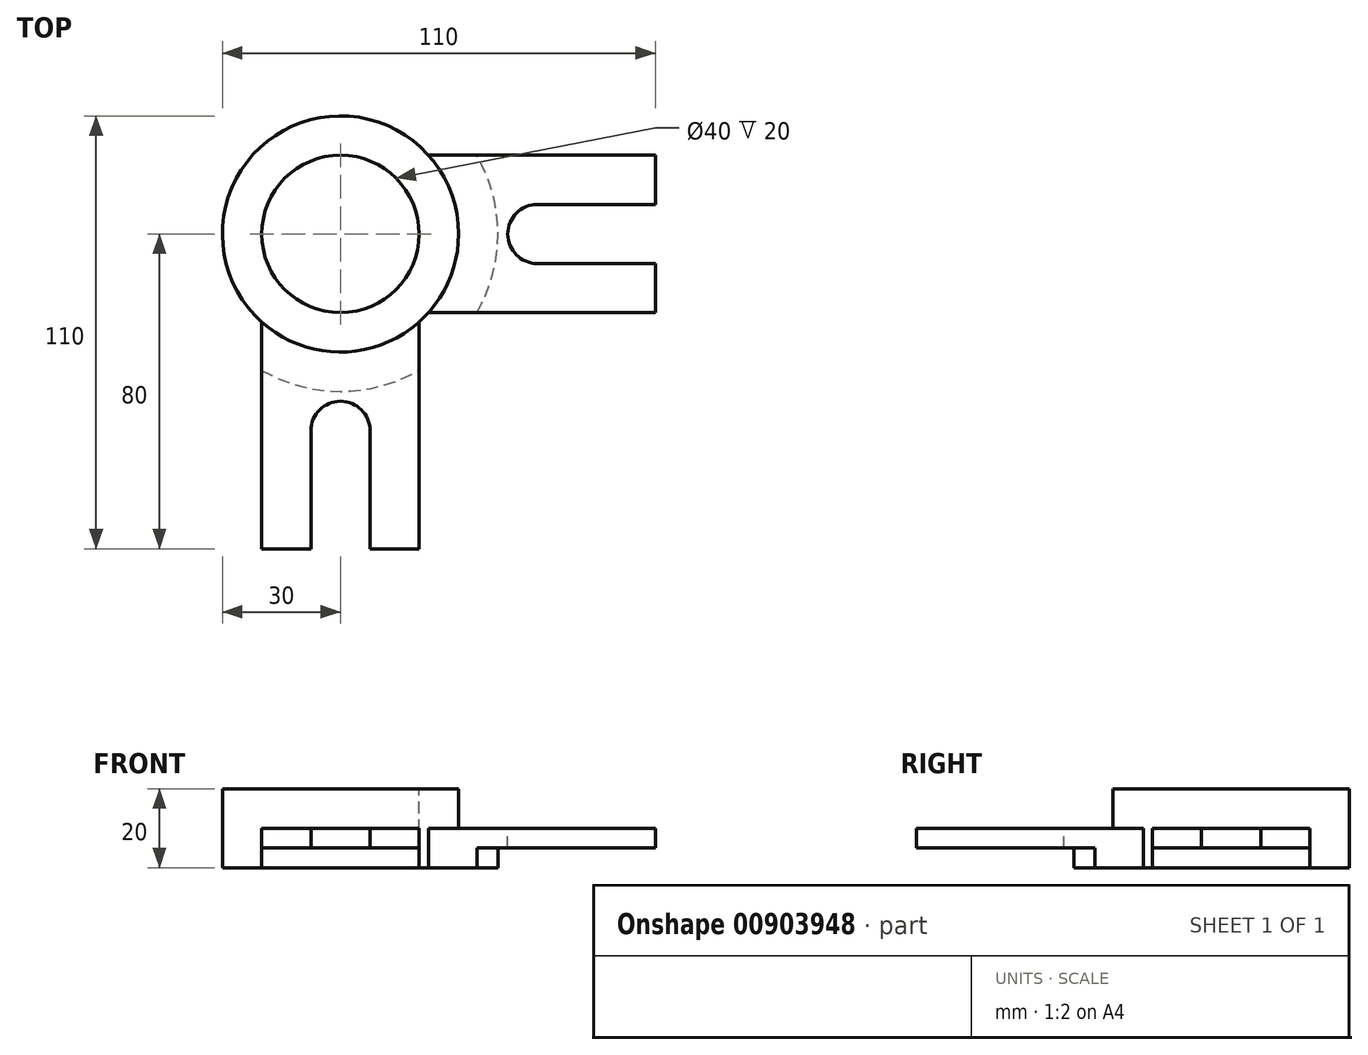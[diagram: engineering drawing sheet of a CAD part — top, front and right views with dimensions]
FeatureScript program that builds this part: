
annotation { "Feature Type Name" : "Feature", "Feature Type Description" : "" }
export const myFeature = defineFeature(function(context is Context, id is Id, definition is map)
    precondition{}
    {
        {
            var Q0;
            Q0=qCreatedBy(makeId("Top.planeOp"),FACE);
            var sketch = newSketch(context, id + "F0", { "sketchPlane" : qUnion([Q0])});
            skCircle(sketch, "E0", {"center": v(0, 0) * mm, "radius": 30 * mm});
            skSolve(sketch);
        }
        {
            var Q0;
            Q0=makeQuery(id+"F0.imprint","IMPRINT",FACE,{"disambiguationData":[TD([[makeQuery(id+"F0.imprint","IMPRINT",EDGE,{"derivedFrom":sQuery(id+"F0.wireOp",EDGE,"E0")}),1.0]])]});
            extrude(context, id + "F1", {"entities" : qUnion([Q0]), "depth" : 20 * mm, "offsetDistance" : 25 * mm});
        }
        {
            var Q0;
            Q0=qCreatedBy(makeId("Top.planeOp"),FACE);
            var sketch = newSketch(context, id + "F2", { "sketchPlane" : qUnion([Q0])});
            skLineSegment(sketch, "E1", {"start": v(0, 0) * mm, "end": v(94.8, 0) * mm, "construction": true});
            skLineSegment(sketch, "E2.bottom", {"start": v(0, 20) * mm, "end": v(80, 20) * mm});
            skLineSegment(sketch, "E2.top", {"start": v(0, -20) * mm, "end": v(80, -20) * mm});
            skLineSegment(sketch, "E2.left", {"start": v(0, 20) * mm, "end": v(0, -20) * mm});
            skLineSegment(sketch, "E2.right", {"start": v(80, 20) * mm, "end": v(80, -20) * mm});
            skSolve(sketch);
        }
        {
            var Q0;
            Q0=makeQuery(id+"F2.imprint","IMPRINT",FACE,{"disambiguationData":[TD([[makeQuery(id+"F2.imprint","IMPRINT",EDGE,{"derivedFrom":sQuery(id+"F2.wireOp",EDGE,"E2.bottom")}),-1.0]])]});
            extrude(context, id + "F3", {"entities" : qUnion([Q0]), "operationType" : NewBodyOperationType.ADD, "depth" : 10 * mm, "offsetDistance" : 25 * mm});
        }
        {
            var Q0;
            Q0=makeQuery(id+"F3.opExtrude","CAP_FACE",FACE,{"disambiguationData":[OSD([sQuery(id+"F2.wireOp",EDGE,"E2.bottom"),sQuery(id+"F2.wireOp",EDGE,"E2.top"),sQuery(id+"F2.wireOp",EDGE,"E2.left"),sQuery(id+"F2.wireOp",EDGE,"E2.right")])],"isStart":false});
            var sketch = newSketch(context, id + "F4", { "sketchPlane" : qUnion([Q0])});
            skLineSegment(sketch, "E3", {"start": v(50, 0) * mm, "end": v(80, 0) * mm, "construction": true});
            skArc(sketch, "E4", {"start": v(50, 7.5) * mm, "mid": v(42.5, 0) * mm, "end": v(50, -7.5) * mm});
            skLineSegment(sketch, "E5", {"start": v(50, 7.5) * mm, "end": v(80, 7.5) * mm});
            skLineSegment(sketch, "E6", {"start": v(50, -7.5) * mm, "end": v(80, -7.5) * mm});
            skSolve(sketch);
        }
        {
            var Q0;
            Q0=makeQuery(id+"F4.imprint","IMPRINT",FACE,{"disambiguationData":[TD([[makeQuery(id+"F4.imprint","IMPRINT",EDGE,{"derivedFrom":sQuery(id+"F4.wireOp",EDGE,"E4")}),1.0]])]});
            extrude(context, id + "F5", {"entities" : qUnion([Q0]), "operationType" : NewBodyOperationType.REMOVE, "endBound" : BoundingType.THROUGH_ALL, "oppositeDirection" : true, "depth" : 25 * mm, "offsetDistance" : 25 * mm});
        }
        {
            var Q0;
            Q0=qCreatedBy(makeId("Top.planeOp"),FACE);
            var sketch = newSketch(context, id + "F6", { "sketchPlane" : qUnion([Q0])});
            skCircle(sketch, "E7", {"center": v(0, 0) * mm, "radius": 40 * mm});
            skCircle(sketch, "E8", {"center": v(0, 0) * mm, "radius": 90 * mm});
            skSolve(sketch);
        }
        {
            var Q0;
            Q0=makeQuery(id+"F6.imprint","IMPRINT",FACE,{"disambiguationData":[TD([[makeQuery(id+"F6.imprint","IMPRINT",EDGE,{"derivedFrom":sQuery(id+"F6.wireOp",EDGE,"E7")}),-1.0]])]});
            extrude(context, id + "F7", {"entities" : qUnion([Q0]), "operationType" : NewBodyOperationType.REMOVE, "depth" : 5 * mm, "offsetDistance" : 25 * mm});
        }
        {
            var Q0;
            Q0=makeQuery(id+"F1.opExtrude","SWEPT_BODY",BODY,{"disambiguationData":[OSD([sQuery(id+"F0.wireOp",EDGE,"E0")])]});
            var Q1;
            Q1=makeQuery(id+"F1.opExtrude","CAP_EDGE",EDGE,{"disambiguationData":[OSD([sQuery(id+"F0.wireOp",EDGE,"E0")])],"isStart":false});
            circularPattern(context, id + "F8", {"operationType" : NewBodyOperationType.ADD, "entities" : qUnion([Q0]), "axis" : qUnion([Q1]), "angle" : 90 * degree, "instanceCount" : 2, "oppositeDirection" : true});
        }
        {
            var Q0;
            Q0=makeQuery(id+"F1.opExtrude","CAP_FACE",FACE,{"disambiguationData":[OSD([sQuery(id+"F0.wireOp",EDGE,"E0")])],"isStart":false});
            var sketch = newSketch(context, id + "F9", { "sketchPlane" : qUnion([Q0])});
            skCircle(sketch, "E9", {"center": v(0, 0) * mm, "radius": 20 * mm});
            skSolve(sketch);
        }
        {
            var Q0;
            Q0=makeQuery(id+"F9.imprint","IMPRINT",FACE,{"disambiguationData":[TD([[makeQuery(id+"F9.imprint","IMPRINT",EDGE,{"derivedFrom":sQuery(id+"F9.wireOp",EDGE,"E9")}),1.0]])]});
            extrude(context, id + "F10", {"entities" : qUnion([Q0]), "operationType" : NewBodyOperationType.REMOVE, "endBound" : BoundingType.THROUGH_ALL, "oppositeDirection" : true, "depth" : 25 * mm, "offsetDistance" : 25 * mm});
        }
    });
